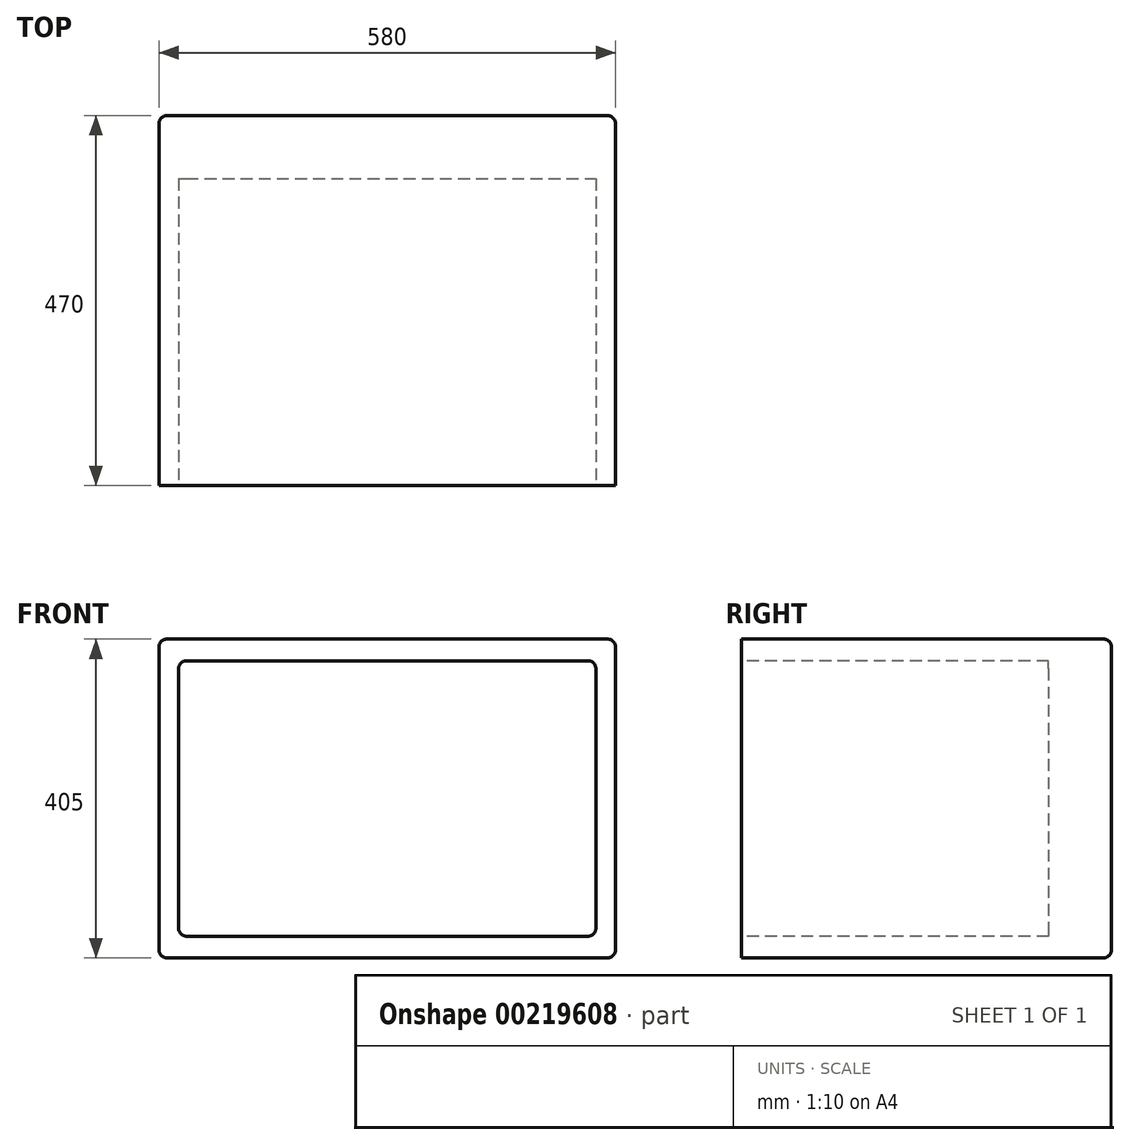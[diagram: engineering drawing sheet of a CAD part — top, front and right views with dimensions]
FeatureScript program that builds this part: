
annotation { "Feature Type Name" : "Feature", "Feature Type Description" : "" }
export const myFeature = defineFeature(function(context is Context, id is Id, definition is map)
    precondition{}
    {
        {
            var Q0;
            Q0=qCreatedBy(makeId("Front.planeOp"),FACE);
            var sketch = newSketch(context, id + "F0", { "sketchPlane" : qUnion([Q0])});
            skLineSegment(sketch, "E0.bottom", {"start": v(-290, 202.5) * mm, "end": v(290, 202.5) * mm});
            skLineSegment(sketch, "E0.top", {"start": v(-290, -202.5) * mm, "end": v(290, -202.5) * mm});
            skLineSegment(sketch, "E0.left", {"start": v(-290, 202.5) * mm, "end": v(-290, -202.5) * mm});
            skLineSegment(sketch, "E0.right", {"start": v(290, 202.5) * mm, "end": v(290, -202.5) * mm});
            skPoint(sketch, "E0.middle", {"position": v(0, 0) * mm});
            skSolve(sketch);
        }
        {
            var Q0;
            Q0=makeQuery(id+"F0.imprint","IMPRINT",FACE,{"disambiguationData":[TD([[makeQuery(id+"F0.imprint","IMPRINT",EDGE,{"derivedFrom":sQuery(id+"F0.wireOp",EDGE,"E0.bottom")}),-1.0]])]});
            extrude(context, id + "F1", {"entities" : qUnion([Q0]), "depth" : 470 * mm});
        }
        {
            var Q0;
            Q0=makeQuery(id+"F1.opExtrude","CAP_FACE",FACE,{"disambiguationData":[OSD([sQuery(id+"F0.wireOp",EDGE,"E0.bottom"),sQuery(id+"F0.wireOp",EDGE,"E0.top"),sQuery(id+"F0.wireOp",EDGE,"E0.left"),sQuery(id+"F0.wireOp",EDGE,"E0.right")])],"isStart":false});
            var sketch = newSketch(context, id + "F2", { "sketchPlane" : qUnion([Q0])});
            skLineSegment(sketch, "E1.bottom", {"start": v(-265, 175) * mm, "end": v(265, 175) * mm});
            skLineSegment(sketch, "E1.top", {"start": v(-265, -175) * mm, "end": v(265, -175) * mm});
            skLineSegment(sketch, "E1.left", {"start": v(-265, 175) * mm, "end": v(-265, -175) * mm});
            skLineSegment(sketch, "E1.right", {"start": v(265, 175) * mm, "end": v(265, -175) * mm});
            skPoint(sketch, "E1.middle", {"position": v(0, 0) * mm});
            skSolve(sketch);
        }
        {
            var Q0;
            Q0=makeQuery(id+"F2.imprint","IMPRINT",FACE,{"disambiguationData":[TD([[makeQuery(id+"F2.imprint","IMPRINT",EDGE,{"derivedFrom":sQuery(id+"F2.wireOp",EDGE,"E1.bottom")}),-1.0]])]});
            extrude(context, id + "F3", {"entities" : qUnion([Q0]), "operationType" : NewBodyOperationType.REMOVE, "oppositeDirection" : true, "depth" : 390 * mm});
        }
        {
            var Q0;
            Q0=makeQuery(id+"F1.opExtrude","SWEPT_EDGE",EDGE,{"disambiguationData":[OSD([sQuery(id+"F0.wireOp",EDGE,"E0.bottom"),sQuery(id+"F0.wireOp",EDGE,"E0.left")])]});
            var Q1;
            Q1=makeQuery(id+"F1.opExtrude","SWEPT_EDGE",EDGE,{"disambiguationData":[OSD([sQuery(id+"F0.wireOp",EDGE,"E0.bottom"),sQuery(id+"F0.wireOp",EDGE,"E0.right")])]});
            var Q2;
            Q2=makeQuery(id+"F1.opExtrude","SWEPT_EDGE",EDGE,{"disambiguationData":[OSD([sQuery(id+"F0.wireOp",EDGE,"E0.top"),sQuery(id+"F0.wireOp",EDGE,"E0.left")])]});
            var Q3;
            Q3=makeQuery(id+"F1.opExtrude","SWEPT_EDGE",EDGE,{"disambiguationData":[OSD([sQuery(id+"F0.wireOp",EDGE,"E0.top"),sQuery(id+"F0.wireOp",EDGE,"E0.right")])]});
            var Q4;
            Q4=makeQuery(id+"F3.boolean.opBoolean","COPY",EDGE,{"derivedFrom":makeQuery(id+"F3.opExtrude","SWEPT_EDGE",EDGE,{"disambiguationData":[OSD([sQuery(id+"F2.wireOp",EDGE,"E1.bottom"),sQuery(id+"F2.wireOp",EDGE,"E1.left")])]})});
            var Q5;
            Q5=makeQuery(id+"F3.boolean.opBoolean","COPY",EDGE,{"derivedFrom":makeQuery(id+"F3.opExtrude","SWEPT_EDGE",EDGE,{"disambiguationData":[OSD([sQuery(id+"F2.wireOp",EDGE,"E1.bottom"),sQuery(id+"F2.wireOp",EDGE,"E1.right")])]})});
            var Q6;
            Q6=makeQuery(id+"F3.boolean.opBoolean","COPY",EDGE,{"derivedFrom":makeQuery(id+"F3.opExtrude","SWEPT_EDGE",EDGE,{"disambiguationData":[OSD([sQuery(id+"F2.wireOp",EDGE,"E1.top"),sQuery(id+"F2.wireOp",EDGE,"E1.right")])]})});
            var Q7;
            Q7=makeQuery(id+"F3.boolean.opBoolean","COPY",EDGE,{"derivedFrom":makeQuery(id+"F3.opExtrude","SWEPT_EDGE",EDGE,{"disambiguationData":[OSD([sQuery(id+"F2.wireOp",EDGE,"E1.top"),sQuery(id+"F2.wireOp",EDGE,"E1.left")])]})});
            var Q8;
            Q8=makeQuery(id+"F1.opExtrude","CAP_EDGE",EDGE,{"disambiguationData":[OSD([sQuery(id+"F0.wireOp",EDGE,"E0.bottom")])],"isStart":true});
            var Q9;
            Q9=makeQuery(id+"F1.opExtrude","CAP_EDGE",EDGE,{"disambiguationData":[OSD([sQuery(id+"F0.wireOp",EDGE,"E0.right")])],"isStart":true});
            var Q10;
            Q10=makeQuery(id+"F1.opExtrude","CAP_EDGE",EDGE,{"disambiguationData":[OSD([sQuery(id+"F0.wireOp",EDGE,"E0.top")])],"isStart":true});
            var Q11;
            Q11=makeQuery(id+"F1.opExtrude","CAP_EDGE",EDGE,{"disambiguationData":[OSD([sQuery(id+"F0.wireOp",EDGE,"E0.left")])],"isStart":true});
            fillet(context, id + "F4", {"entities" : qUnion([Q0, Q1, Q2, Q3, Q4, Q5, Q6, Q7, Q8, Q9, Q10, Q11]), "radius" : 10 * mm, "tangentPropagation" : true, "allowEdgeOverflow" : false});
        }
    });
